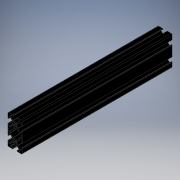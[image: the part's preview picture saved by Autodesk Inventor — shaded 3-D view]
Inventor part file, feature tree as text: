
AUTODESK INVENTOR PART (.ipt)
format: ipt  version: 2019 (Build 230136000, 136)  size: 346,624 bytes
history: native  units: mm
features: extrude x1, sketch x1
ambient origin geometry x8: Origin, YZ Plane, XZ Plane, XY Plane, X Axis, Y Axis, Z Axis, Center Point
bodies: Solid1 (feature_tree)
feature tree (2):
  extrude  "Extrusion1"  [1 undecoded]
  sketch  "Sketch_1"  dims[d0=203.2mm d1=0.0mm]
note: 1 required parameter value undecoded (feature->parameter linkage not recoverable at this tier; creation-order binding heuristic only, values carry confidence <= 0.55)
